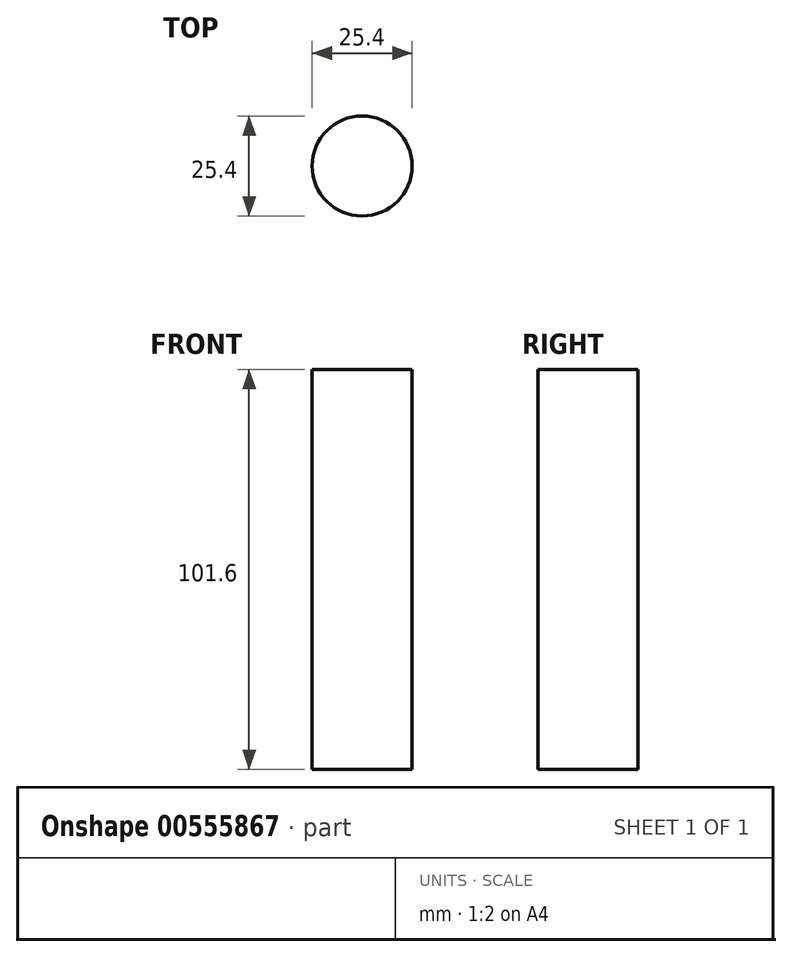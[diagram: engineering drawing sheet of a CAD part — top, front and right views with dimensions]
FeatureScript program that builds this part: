
annotation { "Feature Type Name" : "Feature", "Feature Type Description" : "" }
export const myFeature = defineFeature(function(context is Context, id is Id, definition is map)
    precondition{}
    {
        {
            var Q0;
            Q0=qCreatedBy(makeId("Top.planeOp"),FACE);
            var sketch = newSketch(context, id + "F0", { "sketchPlane" : qUnion([Q0])});
            skCircle(sketch, "E0", {"center": v(0, 0) * mm, "radius": 12.7 * mm});
            skSolve(sketch);
        }
        {
            var Q0;
            Q0 = qSketchRegion(id + "F0", true);
            extrude(context, id + "F1", {"entities" : qUnion([Q0]), "depth" : 101.6 * mm, "offsetDistance" : 25.4 * mm});
        }
    });
